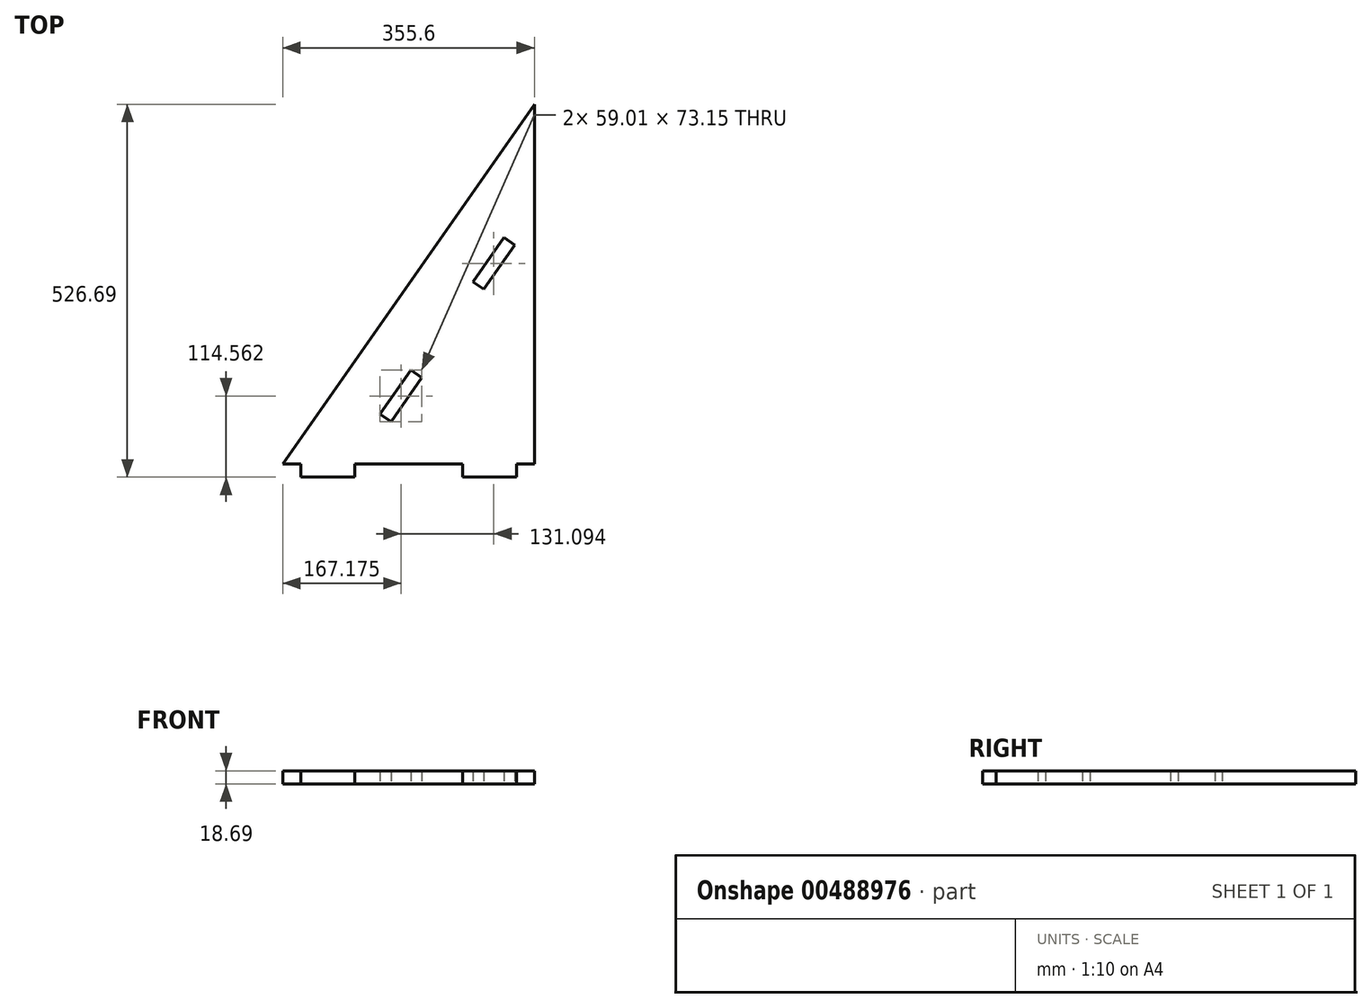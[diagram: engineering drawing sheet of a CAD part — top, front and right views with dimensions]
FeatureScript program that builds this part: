
annotation { "Feature Type Name" : "Feature", "Feature Type Description" : "" }
export const myFeature = defineFeature(function(context is Context, id is Id, definition is map)
    precondition{}
    {
        {
            var Q0;
            Q0=qCreatedBy(makeId("Top.planeOp"),FACE);
            var sketch = newSketch(context, id + "F0", { "sketchPlane" : qUnion([Q0])});
            skLineSegment(sketch, "E0", {"start": v(-312.46, -70.02) * mm, "end": v(-287.06, -70.02) * mm});
            skPoint(sketch, "E1.startSnap0", {"position": v(-134.66, -70.02) * mm});
            skLineSegment(sketch, "E2", {"start": v(-312.46, -70.02) * mm, "end": v(43.14, 437.98) * mm});
            skLineSegment(sketch, "E3", {"start": v(43.14, 437.98) * mm, "end": v(43.14, -70.02) * mm});
            skLineSegment(sketch, "E4", {"start": v(-174.8, 0) * mm, "end": v(-159.48, -10.72) * mm});
            skLineSegment(sketch, "E5", {"start": v(-159.48, -10.72) * mm, "end": v(-115.78, 51.7) * mm});
            skLineSegment(sketch, "E6", {"start": v(15.32, 238.98) * mm, "end": v(0, 249.7) * mm});
            skLineSegment(sketch, "E7", {"start": v(0, 249.7) * mm, "end": v(-43.7, 187.28) * mm});
            skLineSegment(sketch, "E8", {"start": v(-131.1, 62.43) * mm, "end": v(-115.78, 51.7) * mm});
            skLineSegment(sketch, "E9", {"start": v(-43.7, 187.28) * mm, "end": v(-28.38, 176.56) * mm});
            skLineSegment(sketch, "E10.trimOffspring", {"start": v(-131.1, 62.43) * mm, "end": v(-174.8, 0) * mm});
            skLineSegment(sketch, "E11.trimOffspring", {"start": v(-28.38, 176.56) * mm, "end": v(15.32, 238.98) * mm});
            skLineSegment(sketch, "E12", {"start": v(-287.06, -70.02) * mm, "end": v(-287.06, -88.71) * mm});
            skLineSegment(sketch, "E13", {"start": v(-287.06, -88.71) * mm, "end": v(-210.86, -88.71) * mm});
            skLineSegment(sketch, "E14", {"start": v(-210.86, -88.71) * mm, "end": v(-210.86, -70.02) * mm});
            skLineSegment(sketch, "E15", {"start": v(-58.46, -70.02) * mm, "end": v(-58.46, -88.71) * mm});
            skLineSegment(sketch, "E16", {"start": v(-58.46, -88.71) * mm, "end": v(17.74, -88.71) * mm});
            skLineSegment(sketch, "E17", {"start": v(17.74, -88.71) * mm, "end": v(17.74, -70.02) * mm});
            skLineSegment(sketch, "E18.trimOffspring", {"start": v(-210.86, -70.02) * mm, "end": v(-58.46, -70.02) * mm});
            skLineSegment(sketch, "E19.trimOffspring", {"start": v(17.74, -70.02) * mm, "end": v(43.14, -70.02) * mm});
            skSolve(sketch);
        }
        {
            var Q0;
            Q0=makeQuery(id+"F0.imprint","IMPRINT",FACE,{"disambiguationData":[TD([[makeQuery(id+"F0.imprint","IMPRINT",EDGE,{"derivedFrom":sQuery(id+"F0.wireOp",EDGE,"E0")}),1.0]])]});
            extrude(context, id + "F1", {"entities" : qUnion([Q0]), "depth" : 18.7 * mm, "offsetDistance" : 25.4 * mm});
        }
    });
